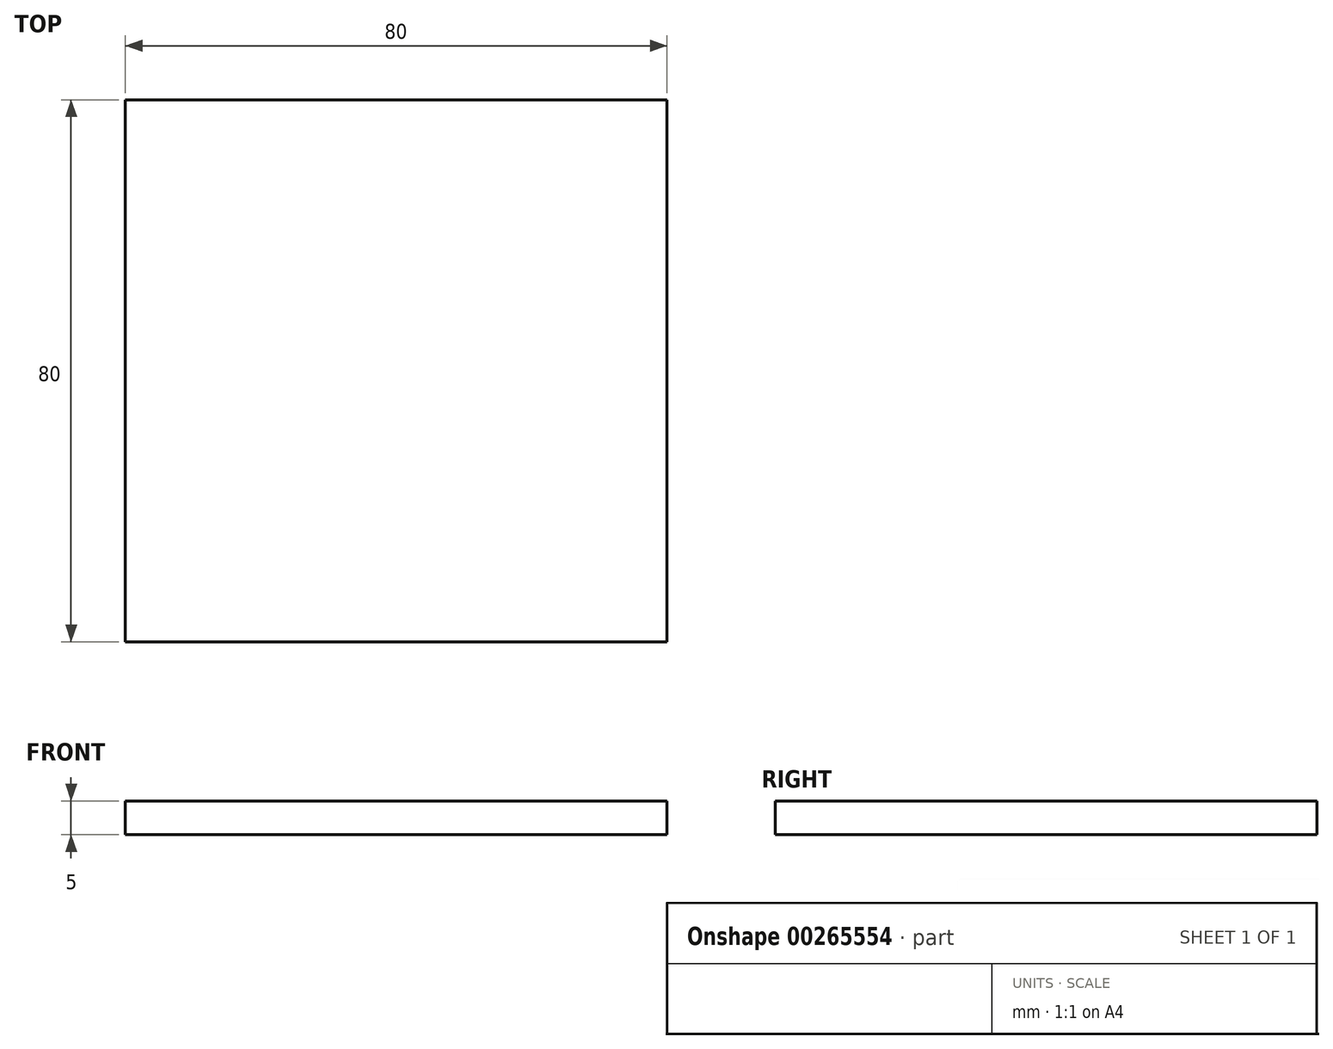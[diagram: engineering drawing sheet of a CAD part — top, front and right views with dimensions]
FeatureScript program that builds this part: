
annotation { "Feature Type Name" : "Feature", "Feature Type Description" : "" }
export const myFeature = defineFeature(function(context is Context, id is Id, definition is map)
    precondition{}
    {
        {
            var Q0;
            Q0=qCreatedBy(makeId("Top.planeOp"),FACE);
            var sketch = newSketch(context, id + "F0", { "sketchPlane" : qUnion([Q0])});
            skLineSegment(sketch, "E0.bottom", {"start": v(-40, 40) * mm, "end": v(40, 40) * mm});
            skLineSegment(sketch, "E0.top", {"start": v(-40, -40) * mm, "end": v(40, -40) * mm});
            skLineSegment(sketch, "E0.left", {"start": v(-40, 40) * mm, "end": v(-40, -40) * mm});
            skLineSegment(sketch, "E0.right", {"start": v(40, 40) * mm, "end": v(40, -40) * mm});
            skLineSegment(sketch, "E1", {"start": v(-40, -40) * mm, "end": v(0, 0) * mm, "construction": true});
            skLineSegment(sketch, "E2", {"start": v(0, 0) * mm, "end": v(40, 40) * mm, "construction": true});
            skSolve(sketch);
        }
        {
            var Q0;
            Q0 = qSketchRegion(id + "F0", true);
            extrude(context, id + "F1", {"entities" : qUnion([Q0]), "depth" : 5 * mm, "offsetDistance" : 25 * mm});
        }
    });
